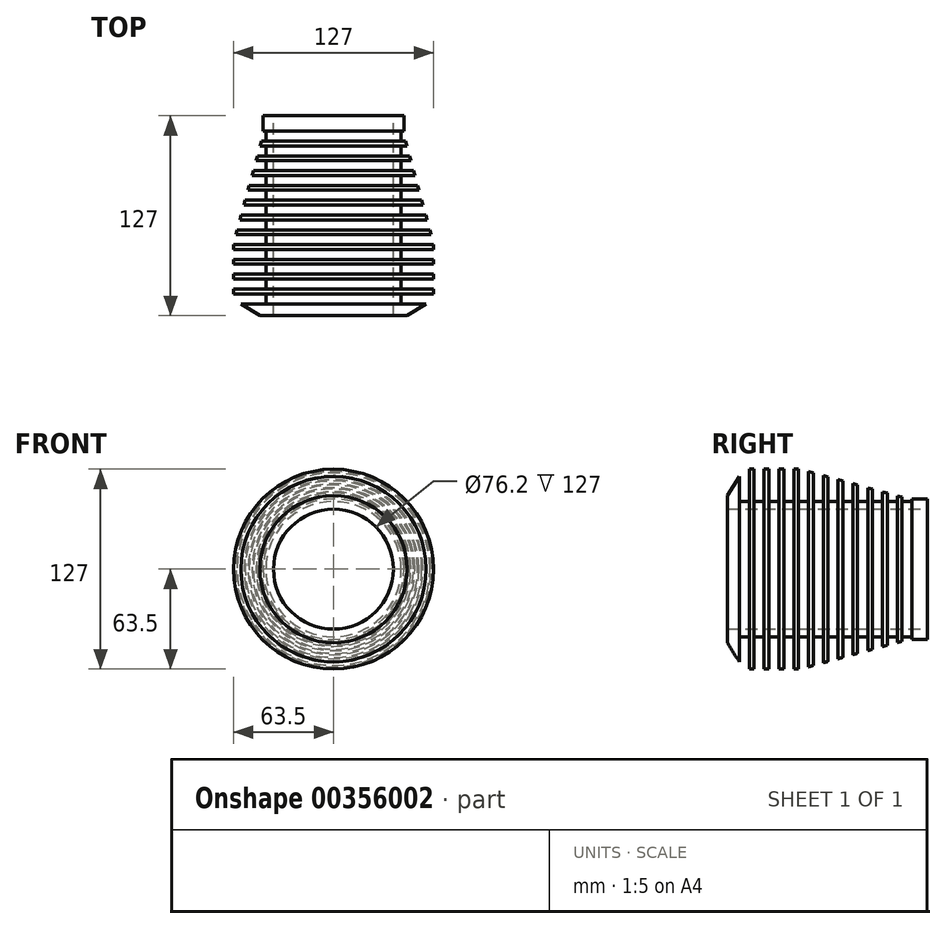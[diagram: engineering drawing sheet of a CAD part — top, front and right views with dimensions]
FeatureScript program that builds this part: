
annotation { "Feature Type Name" : "Feature", "Feature Type Description" : "" }
export const myFeature = defineFeature(function(context is Context, id is Id, definition is map)
    precondition{}
    {
        {
            var Q0;
            Q0=qCreatedBy(makeId("Front.planeOp"),FACE);
            var sketch = newSketch(context, id + "F0", { "sketchPlane" : qUnion([Q0])});
            skCircle(sketch, "E0", {"center": v(0, 0) * mm, "radius": 38.1 * mm});
            skCircle(sketch, "E1", {"center": v(0, 0) * mm, "radius": 63.5 * mm});
            skSolve(sketch);
        }
        {
            var Q0;
            Q0=makeQuery(id+"F0.imprint","IMPRINT",FACE,{"disambiguationData":[TD([[makeQuery(id+"F0.imprint","IMPRINT",EDGE,{"derivedFrom":sQuery(id+"F0.wireOp",EDGE,"E0")}),-1.0]])]});
            extrude(context, id + "F1", {"entities" : qUnion([Q0]), "depth" : 127 * mm});
        }
        {
            var Q0;
            Q0=qCreatedBy(makeId("Right.planeOp"),FACE);
            var sketch = newSketch(context, id + "F2", { "sketchPlane" : qUnion([Q0])});
            skLineSegment(sketch, "E2.bottom", {"start": v(-9.73, 42.96) * mm, "end": v(-16.08, 42.96) * mm});
            skLineSegment(sketch, "E2.top", {"start": v(-9.73, 83.6) * mm, "end": v(-16.08, 83.6) * mm});
            skLineSegment(sketch, "E2.left", {"start": v(-9.73, 42.96) * mm, "end": v(-9.73, 83.6) * mm});
            skLineSegment(sketch, "E2.right", {"start": v(-16.08, 42.96) * mm, "end": v(-16.08, 83.6) * mm});
            skPoint(sketch, "E2.middle", {"position": v(-12.9, 63.28) * mm});
            skLineSegment(sketch, "E3.1.0.0", {"start": v(-19.13, 42.96) * mm, "end": v(-19.13, 83.6) * mm});
            skLineSegment(sketch, "E3.1.0.1", {"start": v(-19.13, 83.6) * mm, "end": v(-25.48, 83.6) * mm});
            skLineSegment(sketch, "E3.1.0.2", {"start": v(-25.48, 42.96) * mm, "end": v(-25.48, 83.6) * mm});
            skLineSegment(sketch, "E3.1.0.3", {"start": v(-19.13, 42.96) * mm, "end": v(-25.48, 42.96) * mm});
            skLineSegment(sketch, "E3.2.0.0", {"start": v(-28.53, 42.96) * mm, "end": v(-28.53, 83.6) * mm});
            skLineSegment(sketch, "E3.2.0.1", {"start": v(-28.53, 83.6) * mm, "end": v(-34.88, 83.6) * mm});
            skLineSegment(sketch, "E3.2.0.2", {"start": v(-34.88, 42.96) * mm, "end": v(-34.88, 83.6) * mm});
            skLineSegment(sketch, "E3.2.0.3", {"start": v(-28.53, 42.96) * mm, "end": v(-34.88, 42.96) * mm});
            skLineSegment(sketch, "E3.3.0.0", {"start": v(-37.93, 42.96) * mm, "end": v(-37.93, 83.6) * mm});
            skLineSegment(sketch, "E3.3.0.1", {"start": v(-37.93, 83.6) * mm, "end": v(-44.28, 83.6) * mm});
            skLineSegment(sketch, "E3.3.0.2", {"start": v(-44.28, 42.96) * mm, "end": v(-44.28, 83.6) * mm});
            skLineSegment(sketch, "E3.3.0.3", {"start": v(-37.93, 42.96) * mm, "end": v(-44.28, 42.96) * mm});
            skLineSegment(sketch, "E3.4.0.0", {"start": v(-47.32, 42.96) * mm, "end": v(-47.32, 83.6) * mm});
            skLineSegment(sketch, "E3.4.0.1", {"start": v(-47.32, 83.6) * mm, "end": v(-53.67, 83.6) * mm});
            skLineSegment(sketch, "E3.4.0.2", {"start": v(-53.67, 42.96) * mm, "end": v(-53.67, 83.6) * mm});
            skLineSegment(sketch, "E3.4.0.3", {"start": v(-47.32, 42.96) * mm, "end": v(-53.67, 42.96) * mm});
            skLineSegment(sketch, "E3.5.0.0", {"start": v(-56.72, 42.96) * mm, "end": v(-56.72, 83.6) * mm});
            skLineSegment(sketch, "E3.5.0.1", {"start": v(-56.72, 83.6) * mm, "end": v(-63.07, 83.6) * mm});
            skLineSegment(sketch, "E3.5.0.2", {"start": v(-63.07, 42.96) * mm, "end": v(-63.07, 83.6) * mm});
            skLineSegment(sketch, "E3.5.0.3", {"start": v(-56.72, 42.96) * mm, "end": v(-63.07, 42.96) * mm});
            skLineSegment(sketch, "E3.6.0.0", {"start": v(-66.12, 42.96) * mm, "end": v(-66.12, 83.6) * mm});
            skLineSegment(sketch, "E3.6.0.1", {"start": v(-66.12, 83.6) * mm, "end": v(-72.47, 83.6) * mm});
            skLineSegment(sketch, "E3.6.0.2", {"start": v(-72.47, 42.96) * mm, "end": v(-72.47, 83.6) * mm});
            skLineSegment(sketch, "E3.6.0.3", {"start": v(-66.12, 42.96) * mm, "end": v(-72.47, 42.96) * mm});
            skLineSegment(sketch, "E3.7.0.0", {"start": v(-75.52, 42.96) * mm, "end": v(-75.52, 83.6) * mm});
            skLineSegment(sketch, "E3.7.0.1", {"start": v(-75.52, 83.6) * mm, "end": v(-81.87, 83.6) * mm});
            skLineSegment(sketch, "E3.7.0.2", {"start": v(-81.87, 42.96) * mm, "end": v(-81.87, 83.6) * mm});
            skLineSegment(sketch, "E3.7.0.3", {"start": v(-75.52, 42.96) * mm, "end": v(-81.87, 42.96) * mm});
            skLineSegment(sketch, "E3.8.0.0", {"start": v(-84.92, 42.96) * mm, "end": v(-84.92, 83.6) * mm});
            skLineSegment(sketch, "E3.8.0.1", {"start": v(-84.92, 83.6) * mm, "end": v(-91.27, 83.6) * mm});
            skLineSegment(sketch, "E3.8.0.2", {"start": v(-91.27, 42.96) * mm, "end": v(-91.27, 83.6) * mm});
            skLineSegment(sketch, "E3.8.0.3", {"start": v(-84.92, 42.96) * mm, "end": v(-91.27, 42.96) * mm});
            skLineSegment(sketch, "E3.9.0.0", {"start": v(-94.31, 42.96) * mm, "end": v(-94.31, 83.6) * mm});
            skLineSegment(sketch, "E3.9.0.1", {"start": v(-94.31, 83.6) * mm, "end": v(-100.66, 83.6) * mm});
            skLineSegment(sketch, "E3.9.0.2", {"start": v(-100.66, 42.96) * mm, "end": v(-100.66, 83.6) * mm});
            skLineSegment(sketch, "E3.9.0.3", {"start": v(-94.31, 42.96) * mm, "end": v(-100.66, 42.96) * mm});
            skLineSegment(sketch, "E3.10.0.0", {"start": v(-103.71, 42.96) * mm, "end": v(-103.71, 83.6) * mm});
            skLineSegment(sketch, "E3.10.0.1", {"start": v(-103.71, 83.6) * mm, "end": v(-110.06, 83.6) * mm});
            skLineSegment(sketch, "E3.10.0.2", {"start": v(-110.06, 42.96) * mm, "end": v(-110.06, 83.6) * mm});
            skLineSegment(sketch, "E3.10.0.3", {"start": v(-103.71, 42.96) * mm, "end": v(-110.06, 42.96) * mm});
            skLineSegment(sketch, "E3.11.0.0", {"start": v(-113.11, 42.96) * mm, "end": v(-113.11, 83.6) * mm});
            skLineSegment(sketch, "E3.11.0.1", {"start": v(-113.11, 83.6) * mm, "end": v(-119.46, 83.6) * mm});
            skLineSegment(sketch, "E3.11.0.2", {"start": v(-119.46, 42.96) * mm, "end": v(-119.46, 83.6) * mm});
            skLineSegment(sketch, "E3.11.0.3", {"start": v(-113.11, 42.96) * mm, "end": v(-119.46, 42.96) * mm});
            skLineSegment(sketch, "E3.direction1", {"start": v(-16.08, 42.96) * mm, "end": v(-25.48, 42.96) * mm, "construction": true});
            skSolve(sketch);
        }
        {
            var Q0;
            Q0=makeQuery(id+"F2.imprint","IMPRINT",FACE,{"disambiguationData":[TD([[makeQuery(id+"F2.imprint","IMPRINT",EDGE,{"derivedFrom":sQuery(id+"F2.wireOp",EDGE,"E2.bottom")}),-1.0]])]});
            var Q1;
            Q1=makeQuery(id+"F2.imprint","IMPRINT",FACE,{"disambiguationData":[TD([[makeQuery(id+"F2.imprint","IMPRINT",EDGE,{"derivedFrom":sQuery(id+"F2.wireOp",EDGE,"E3.1.0.0")}),1.0]])]});
            var Q2;
            Q2=makeQuery(id+"F2.imprint","IMPRINT",FACE,{"disambiguationData":[TD([[makeQuery(id+"F2.imprint","IMPRINT",EDGE,{"derivedFrom":sQuery(id+"F2.wireOp",EDGE,"E3.2.0.0")}),1.0]])]});
            var Q3;
            Q3=makeQuery(id+"F2.imprint","IMPRINT",FACE,{"disambiguationData":[TD([[makeQuery(id+"F2.imprint","IMPRINT",EDGE,{"derivedFrom":sQuery(id+"F2.wireOp",EDGE,"E3.3.0.0")}),1.0]])]});
            var Q4;
            Q4=makeQuery(id+"F2.imprint","IMPRINT",FACE,{"disambiguationData":[TD([[makeQuery(id+"F2.imprint","IMPRINT",EDGE,{"derivedFrom":sQuery(id+"F2.wireOp",EDGE,"E3.4.0.0")}),1.0]])]});
            var Q5;
            Q5=makeQuery(id+"F2.imprint","IMPRINT",FACE,{"disambiguationData":[TD([[makeQuery(id+"F2.imprint","IMPRINT",EDGE,{"derivedFrom":sQuery(id+"F2.wireOp",EDGE,"E3.5.0.0")}),1.0]])]});
            var Q6;
            Q6=makeQuery(id+"F2.imprint","IMPRINT",FACE,{"disambiguationData":[TD([[makeQuery(id+"F2.imprint","IMPRINT",EDGE,{"derivedFrom":sQuery(id+"F2.wireOp",EDGE,"E3.6.0.0")}),1.0]])]});
            var Q7;
            Q7=makeQuery(id+"F2.imprint","IMPRINT",FACE,{"disambiguationData":[TD([[makeQuery(id+"F2.imprint","IMPRINT",EDGE,{"derivedFrom":sQuery(id+"F2.wireOp",EDGE,"E3.7.0.0")}),1.0]])]});
            var Q8;
            Q8=makeQuery(id+"F2.imprint","IMPRINT",FACE,{"disambiguationData":[TD([[makeQuery(id+"F2.imprint","IMPRINT",EDGE,{"derivedFrom":sQuery(id+"F2.wireOp",EDGE,"E3.8.0.0")}),1.0]])]});
            var Q9;
            Q9=makeQuery(id+"F2.imprint","IMPRINT",FACE,{"disambiguationData":[TD([[makeQuery(id+"F2.imprint","IMPRINT",EDGE,{"derivedFrom":sQuery(id+"F2.wireOp",EDGE,"E3.9.0.0")}),1.0]])]});
            var Q10;
            Q10=makeQuery(id+"F2.imprint","IMPRINT",FACE,{"disambiguationData":[TD([[makeQuery(id+"F2.imprint","IMPRINT",EDGE,{"derivedFrom":sQuery(id+"F2.wireOp",EDGE,"E3.10.0.0")}),1.0]])]});
            var Q11;
            Q11=makeQuery(id+"F2.imprint","IMPRINT",FACE,{"disambiguationData":[TD([[makeQuery(id+"F2.imprint","IMPRINT",EDGE,{"derivedFrom":sQuery(id+"F2.wireOp",EDGE,"E3.11.0.0")}),1.0]])]});
            var Q12;
            Q12=makeQuery(id+"F1.opExtrude","CAP_EDGE",EDGE,{"disambiguationData":[OSD([sQuery(id+"F0.wireOp",EDGE,"E1")])],"isStart":true});
            revolve(context, id + "F3", {"operationType" : NewBodyOperationType.REMOVE, "entities" : qUnion([Q0, Q1, Q2, Q3, Q4, Q5, Q6, Q7, Q8, Q9, Q10, Q11]), "axis" : qUnion([Q12]), "revolveType" : RevolveType.FULL, "oppositeDirection" : true});
        }
        {
            var Q0;
            Q0=qCreatedBy(makeId("Right.planeOp"),FACE);
            var sketch = newSketch(context, id + "F4", { "sketchPlane" : qUnion([Q0])});
            skLineSegment(sketch, "E4", {"start": v(-132.08, 38.65) * mm, "end": v(-114.97, 66.03) * mm});
            skLineSegment(sketch, "E5", {"start": v(-114.97, 66.03) * mm, "end": v(-90.15, 66.03) * mm});
            skLineSegment(sketch, "E6", {"start": v(-90.15, 66.03) * mm, "end": v(-12, 44.64) * mm});
            skLineSegment(sketch, "E7", {"start": v(-12, 44.64) * mm, "end": v(6.55, 44.64) * mm});
            skLineSegment(sketch, "E8", {"start": v(6.55, 44.64) * mm, "end": v(6.55, 68.6) * mm});
            skLineSegment(sketch, "E9", {"start": v(6.55, 68.6) * mm, "end": v(-137.78, 68.6) * mm});
            skLineSegment(sketch, "E10", {"start": v(-137.78, 68.6) * mm, "end": v(-132.08, 38.65) * mm});
            skSolve(sketch);
        }
        {
            var Q0;
            Q0=qSketchRegion(id+"F4",true);
            var Q1;
            Q1=makeQuery(id+"F1.opExtrude","CAP_EDGE",EDGE,{"disambiguationData":[OSD([sQuery(id+"F0.wireOp",EDGE,"E1")])],"isStart":false});
            revolve(context, id + "F5", {"operationType" : NewBodyOperationType.REMOVE, "entities" : qUnion([Q0]), "axis" : qUnion([Q1]), "revolveType" : RevolveType.FULL, "oppositeDirection" : true});
        }
    });
